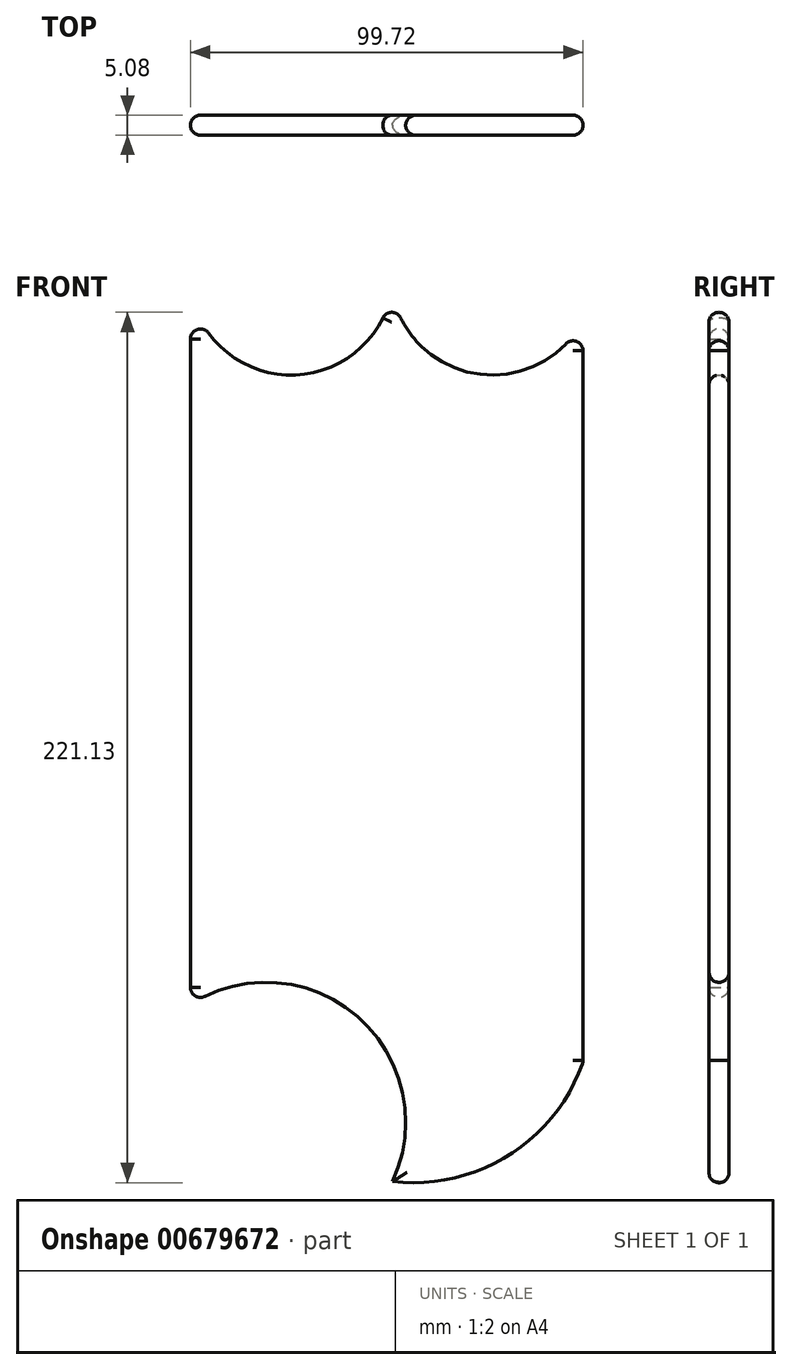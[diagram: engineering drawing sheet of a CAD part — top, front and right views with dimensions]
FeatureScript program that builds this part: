
annotation { "Feature Type Name" : "Feature", "Feature Type Description" : "" }
export const myFeature = defineFeature(function(context is Context, id is Id, definition is map)
    precondition{}
    {
        {
            var Q0;
            Q0=qCreatedBy(makeId("Front.planeOp"),FACE);
            var sketch = newSketch(context, id + "F0", { "sketchPlane" : qUnion([Q0])});
            skLineSegment(sketch, "E0", {"start": v(-51.13, 54.53) * mm, "end": v(-51.13, -126.93) * mm});
            skLineSegment(sketch, "E1.MirrorCS", {"start": v(51.13, 54.53) * mm, "end": v(51.13, -126.93) * mm});
            skArc(sketch, "E2", {"start": v(0.18, -171.9) * mm, "mid": v(-8.56, -130.12) * mm, "end": v(-51.13, -126.93) * mm});
            skArc(sketch, "E3", {"start": v(0.18, -171.9) * mm, "mid": v(35.7, -160.8) * mm, "end": v(51.13, -126.93) * mm});
            skArc(sketch, "E4", {"start": v(-51.13, 54.53) * mm, "mid": v(-25.57, 32.98) * mm, "end": v(0, 54.53) * mm});
            skArc(sketch, "E5.MirrorCS", {"start": v(51.13, 54.53) * mm, "mid": v(25.57, 32.98) * mm, "end": v(0, 54.53) * mm});
            skSolve(sketch);
        }
        {
            var Q0;
            Q0=makeQuery(id+"F0.imprint","IMPRINT",FACE,{"disambiguationData":[TD([[makeQuery(id+"F0.imprint","IMPRINT",EDGE,{"derivedFrom":sQuery(id+"F0.wireOp",EDGE,"E0")}),1.0]])]});
            extrude(context, id + "F1", {"entities" : qUnion([Q0]), "depth" : 5.08 * mm, "offsetDistance" : 25.4 * mm});
        }
        {
            var Q0;
            Q0=makeQuery(id+"F1.opExtrude","CAP_EDGE",EDGE,{"disambiguationData":[OSD([sQuery(id+"F0.wireOp",EDGE,"E1.MirrorCS")])],"isStart":false});
            fillet(context, id + "F2", {"entities" : qUnion([Q0]), "radius" : 5.08 * mm, "tangentPropagation" : true, "allowEdgeOverflow" : false});
        }
        {
            var Q0;
            {var subQ0=sQuery(id+"F0.wireOp",EDGE,"E1.MirrorCS");Q0=makeQuery(id+"F2.opFillet","BLEND_EDGE",EDGE,{"blendedFrom":[makeQuery(id+"F1.opExtrude","CAP_EDGE",EDGE,{"disambiguationData":[OSD([subQ0])],"isStart":false}),makeQuery(id+"F1.opExtrude","CAP_FACE",FACE,{"disambiguationData":[OSD([sQuery(id+"F0.wireOp",EDGE,"E0"),subQ0,sQuery(id+"F0.wireOp",EDGE,"E2"),sQuery(id+"F0.wireOp",EDGE,"E3"),sQuery(id+"F0.wireOp",EDGE,"E4"),sQuery(id+"F0.wireOp",EDGE,"E5.MirrorCS")])],"isStart":true})],"blendedInto":[makeQuery(id+"F1.opExtrude","CAP_FACE",FACE,{"disambiguationData":[OSD([sQuery(id+"F0.wireOp",EDGE,"E0"),subQ0,sQuery(id+"F0.wireOp",EDGE,"E2"),sQuery(id+"F0.wireOp",EDGE,"E3"),sQuery(id+"F0.wireOp",EDGE,"E4"),sQuery(id+"F0.wireOp",EDGE,"E5.MirrorCS")])],"isStart":true})]});}
            fillet(context, id + "F3", {"entities" : qUnion([Q0]), "radius" : 2.54 * mm, "tangentPropagation" : true, "allowEdgeOverflow" : false});
        }
        {
            var Q0;
            Q0=makeQuery(id+"F1.opExtrude","CAP_EDGE",EDGE,{"disambiguationData":[OSD([sQuery(id+"F0.wireOp",EDGE,"E0")])],"isStart":true});
            var Q1;
            Q1=makeQuery(id+"F1.opExtrude","CAP_EDGE",EDGE,{"disambiguationData":[OSD([sQuery(id+"F0.wireOp",EDGE,"E0")])],"isStart":false});
            fillet(context, id + "F4", {"entities" : qUnion([Q0, Q1]), "radius" : 2.54 * mm, "tangentPropagation" : true, "allowEdgeOverflow" : false});
        }
        {
            var Q0;
            Q0=makeQuery(id+"F1.opExtrude","CAP_EDGE",EDGE,{"disambiguationData":[OSD([sQuery(id+"F0.wireOp",EDGE,"E4")])],"isStart":false});
            fillet(context, id + "F5", {"entities" : qUnion([Q0]), "radius" : 2.54 * mm, "tangentPropagation" : true, "allowEdgeOverflow" : false});
        }
        {
            var Q0;
            Q0=makeQuery(id+"F1.opExtrude","CAP_EDGE",EDGE,{"disambiguationData":[OSD([sQuery(id+"F0.wireOp",EDGE,"E5.MirrorCS")])],"isStart":false});
            fillet(context, id + "F6", {"entities" : qUnion([Q0]), "radius" : 2.54 * mm, "tangentPropagation" : true, "allowEdgeOverflow" : false});
        }
        {
            var Q0;
            Q0=makeQuery(id+"F1.opExtrude","CAP_EDGE",EDGE,{"disambiguationData":[OSD([sQuery(id+"F0.wireOp",EDGE,"E2")])],"isStart":false});
            var Q1;
            Q1=makeQuery(id+"F1.opExtrude","CAP_EDGE",EDGE,{"disambiguationData":[OSD([sQuery(id+"F0.wireOp",EDGE,"E3")])],"isStart":false});
            fillet(context, id + "F7", {"entities" : qUnion([Q0, Q1]), "radius" : 2.54 * mm, "tangentPropagation" : true, "allowEdgeOverflow" : false});
        }
    });
